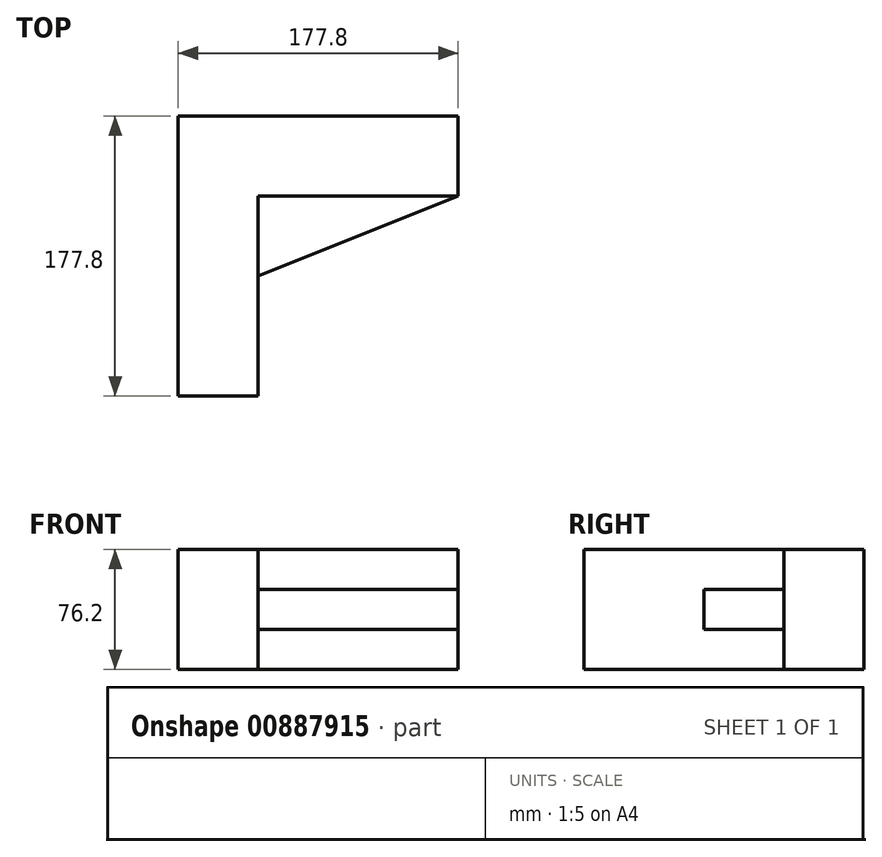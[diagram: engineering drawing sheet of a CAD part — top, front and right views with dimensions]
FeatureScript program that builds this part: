
annotation { "Feature Type Name" : "Feature", "Feature Type Description" : "" }
export const myFeature = defineFeature(function(context is Context, id is Id, definition is map)
    precondition{}
    {
        {
            var Q0;
            Q0=qCreatedBy(makeId("Top.planeOp"),FACE);
            var sketch = newSketch(context, id + "F0", { "sketchPlane" : qUnion([Q0])});
            skLineSegment(sketch, "E0.bottom", {"start": v(0, 0) * mm, "end": v(-50.8, 0) * mm});
            skLineSegment(sketch, "E0.top", {"start": v(0, 177.8) * mm, "end": v(-50.8, 177.8) * mm});
            skLineSegment(sketch, "E0.left", {"start": v(0, 0) * mm, "end": v(0, 177.8) * mm});
            skLineSegment(sketch, "E0.right", {"start": v(-50.8, 0) * mm, "end": v(-50.8, 177.8) * mm});
            skLineSegment(sketch, "E1.bottom", {"start": v(-50.8, 177.8) * mm, "end": v(127, 177.8) * mm});
            skLineSegment(sketch, "E1.top", {"start": v(-50.8, 127) * mm, "end": v(127, 127) * mm});
            skLineSegment(sketch, "E1.left", {"start": v(-50.8, 177.8) * mm, "end": v(-50.8, 127) * mm});
            skLineSegment(sketch, "E1.right", {"start": v(127, 177.8) * mm, "end": v(127, 127) * mm});
            skSolve(sketch);
        }
        {
            var Q0;
            Q0 = qSketchRegion(id + "F0", true);
            extrude(context, id + "F1", {"entities" : qUnion([Q0]), "depth" : 76.2 * mm, "offsetDistance" : 25.4 * mm});
        }
        {
            var Q0;
            Q0=makeQuery(id+"F1.opExtrude","SWEPT_FACE",FACE,{"disambiguationData":[OSD([sQuery(id+"F0.wireOp",EDGE,"E1.top")])]});
            var sketch = newSketch(context, id + "F2", { "sketchPlane" : qUnion([Q0])});
            skLineSegment(sketch, "E2", {"start": v(0, 76.2) * mm, "end": v(0, 50.8) * mm});
            skSolve(sketch);
        }
        {
            var Q0;
            Q0=qCreatedBy(makeId("Top.planeOp"),FACE);
            var Q1;
            Q1=sQuery(id+"F2.wireOp",VERTEX,"E2.end");
            cPlane(context, id + "F3", {"entities" : qUnion([Q0, Q1]), "cplaneType" : CPlaneType.PLANE_POINT, "offset" : 25.4 * mm, "width" : 152.4 * mm, "height" : 152.4 * mm});
        }
        {
            var Q0;
            Q0=qCreatedBy(id+"F3.planeOp",FACE);
            var sketch = newSketch(context, id + "F4", { "sketchPlane" : qUnion([Q0])});
            skPoint(sketch, "E3.0", {"position": v(0, 127) * mm});
            skLineSegment(sketch, "E4", {"start": v(0, 127) * mm, "end": v(0, 76.2) * mm});
            skLineSegment(sketch, "E5", {"start": v(0, 76.2) * mm, "end": v(127, 127) * mm});
            skLineSegment(sketch, "E6", {"start": v(127, 127) * mm, "end": v(0, 127) * mm});
            skSolve(sketch);
        }
        {
            var Q0;
            Q0 = qSketchRegion(id + "F4", true);
            extrude(context, id + "F5", {"entities" : qUnion([Q0]), "oppositeDirection" : true, "depth" : 25.4 * mm, "offsetDistance" : 25.4 * mm});
        }
    });
